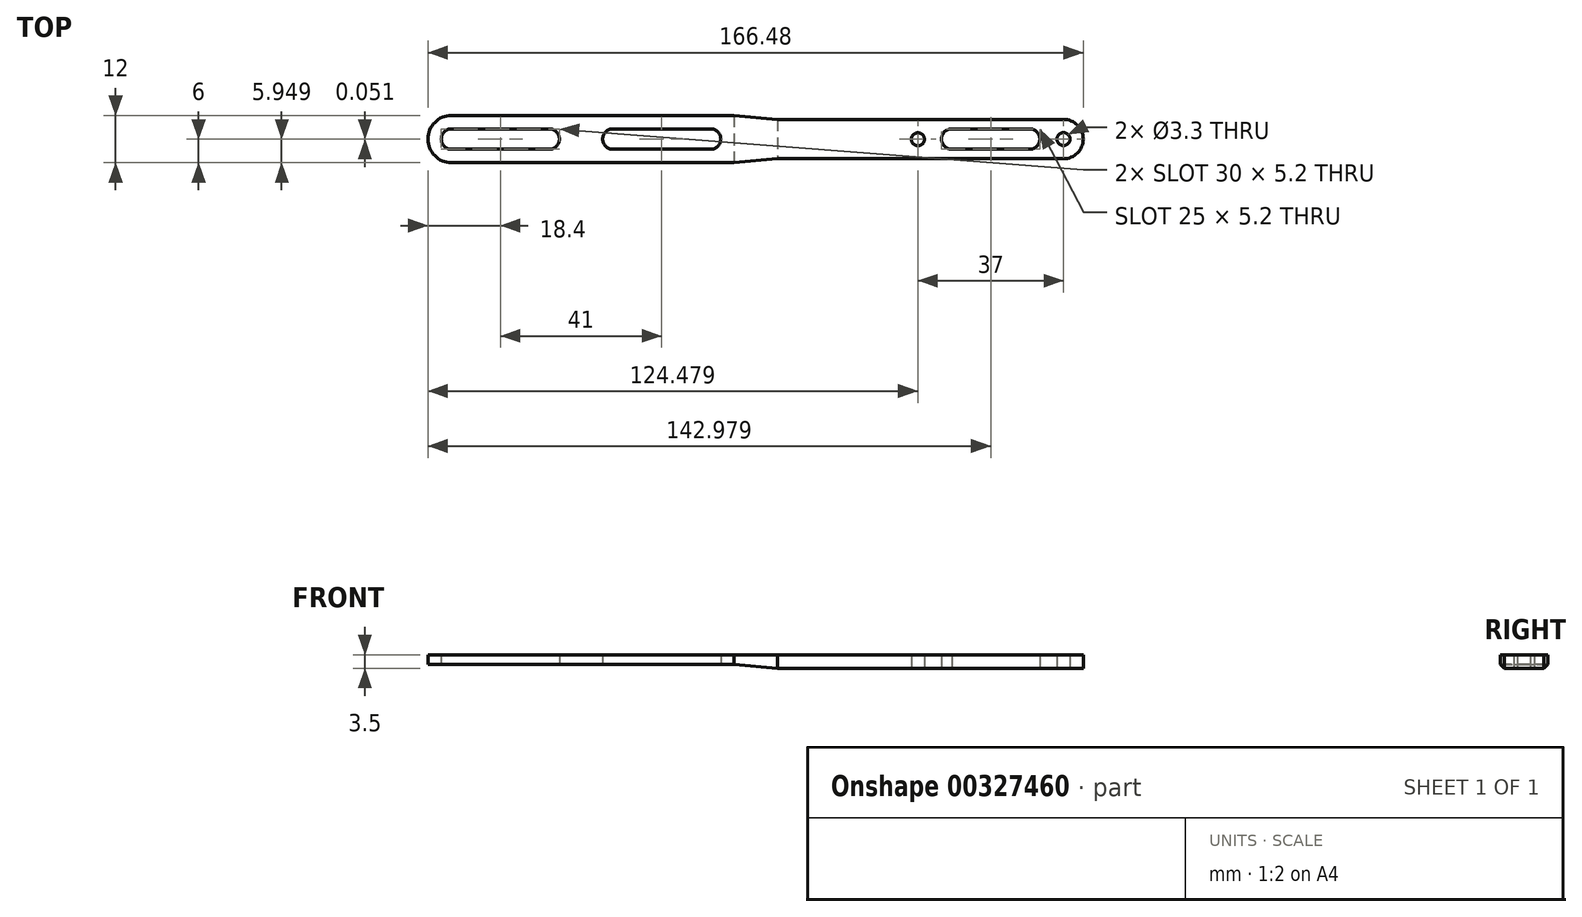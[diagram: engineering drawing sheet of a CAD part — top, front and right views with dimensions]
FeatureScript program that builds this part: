
annotation { "Feature Type Name" : "Feature", "Feature Type Description" : "" }
export const myFeature = defineFeature(function(context is Context, id is Id, definition is map)
    precondition{}
    {
        {
            var Q0;
            Q0=qCreatedBy(makeId("Top.planeOp"),FACE);
            var sketch = newSketch(context, id + "F0", { "sketchPlane" : qUnion([Q0])});
            skCircle(sketch, "E0", {"center": v(46.68, -0.05) * mm, "radius": 1.65 * mm});
            skCircle(sketch, "E1", {"center": v(83.68, 0) * mm, "radius": 1.65 * mm});
            skLineSegment(sketch, "E2", {"start": v(-104.54, 0) * mm, "end": v(102.54, 0) * mm, "construction": true});
            skArc(sketch, "E3", {"start": v(-71.8, 6) * mm, "mid": v(-77.8, 0) * mm, "end": v(-71.8, -6) * mm});
            skArc(sketch, "E4", {"start": v(-71.8, 2.6) * mm, "mid": v(-74.4, 0) * mm, "end": v(-71.8, -2.6) * mm});
            skArc(sketch, "E5", {"start": v(-47, -2.6) * mm, "mid": v(-44.4, 0) * mm, "end": v(-47, 2.6) * mm});
            skArc(sketch, "E6", {"start": v(-30.8, 2.6) * mm, "mid": v(-33.4, 0) * mm, "end": v(-30.8, -2.6) * mm});
            skArc(sketch, "E7", {"start": v(-6, -2.6) * mm, "mid": v(-3.4, 0) * mm, "end": v(-6, 2.6) * mm});
            skArc(sketch, "E8", {"start": v(83.68, -5) * mm, "mid": v(88.68, 0) * mm, "end": v(83.68, 5) * mm});
            skLineSegment(sketch, "E9", {"start": v(-71.8, 2.6) * mm, "end": v(-47, 2.6) * mm});
            skLineSegment(sketch, "E10", {"start": v(-71.8, -2.6) * mm, "end": v(-47, -2.6) * mm});
            skArc(sketch, "E11", {"start": v(75.08, -2.6) * mm, "mid": v(77.68, 0) * mm, "end": v(75.08, 2.6) * mm});
            skArc(sketch, "E12", {"start": v(55.32, 2.6) * mm, "mid": v(52.68, 0.01) * mm, "end": v(55.3, -2.6) * mm});
            skLineSegment(sketch, "E13", {"start": v(55.32, 2.6) * mm, "end": v(75.08, 2.6) * mm});
            skLineSegment(sketch, "E14", {"start": v(55.27, -2.6) * mm, "end": v(75.08, -2.6) * mm});
            skLineSegment(sketch, "E15.trimOffspring", {"start": v(-30.8, 2.6) * mm, "end": v(-6, 2.6) * mm});
            skLineSegment(sketch, "E16.trimOffspring", {"start": v(-30.8, -2.6) * mm, "end": v(-6, -2.6) * mm});
            skLineSegment(sketch, "E17", {"start": v(11, 5) * mm, "end": v(83.68, 5) * mm});
            skLineSegment(sketch, "E18", {"start": v(11, -5) * mm, "end": v(83.68, -5) * mm});
            skLineSegment(sketch, "E19", {"start": v(-12.18, 6) * mm, "end": v(-12.18, 6) * mm});
            skLineSegment(sketch, "E20", {"start": v(-71.8, 6) * mm, "end": v(0, 6) * mm});
            skLineSegment(sketch, "E21", {"start": v(-71.8, -6) * mm, "end": v(0, -6) * mm});
            skLineSegment(sketch, "E22", {"start": v(0, -6) * mm, "end": v(11, -5) * mm});
            skLineSegment(sketch, "E23", {"start": v(0, 6) * mm, "end": v(11, 5) * mm});
            skLineSegment(sketch, "E24", {"start": v(11, -10.94) * mm, "end": v(11, 10.77) * mm, "construction": true});
            skSolve(sketch);
        }
        {
            var Q0;
            Q0=makeQuery(id+"F0.imprint","IMPRINT",FACE,{"disambiguationData":[TD([[makeQuery(id+"F0.imprint","IMPRINT",EDGE,{"derivedFrom":sQuery(id+"F0.wireOp",EDGE,"E0")}),-1.0]])]});
            extrude(context, id + "F1", {"entities" : qUnion([Q0]), "depth" : 3.5 * mm});
        }
        {
            var Q0;
            Q0=qCreatedBy(makeId("Front.planeOp"),FACE);
            var sketch = newSketch(context, id + "F2", { "sketchPlane" : qUnion([Q0])});
            skLineSegment(sketch, "E25", {"start": v(-80.44, 0) * mm, "end": v(-80.44, 1) * mm});
            skLineSegment(sketch, "E26", {"start": v(-80.44, 1) * mm, "end": v(0, 1) * mm});
            skLineSegment(sketch, "E27", {"start": v(0, 1) * mm, "end": v(11, 0) * mm});
            skLineSegment(sketch, "E28", {"start": v(11, 0) * mm, "end": v(-80.44, 0) * mm});
            skSolve(sketch);
        }
        {
            var Q0;
            Q0 = qSketchRegion(id + "F2", true);
            extrude(context, id + "F3", {"entities" : qUnion([Q0]), "operationType" : NewBodyOperationType.REMOVE, "endBound" : BoundingType.SYMMETRIC, "oppositeDirection" : true, "depth" : 12 * mm});
        }
    });
